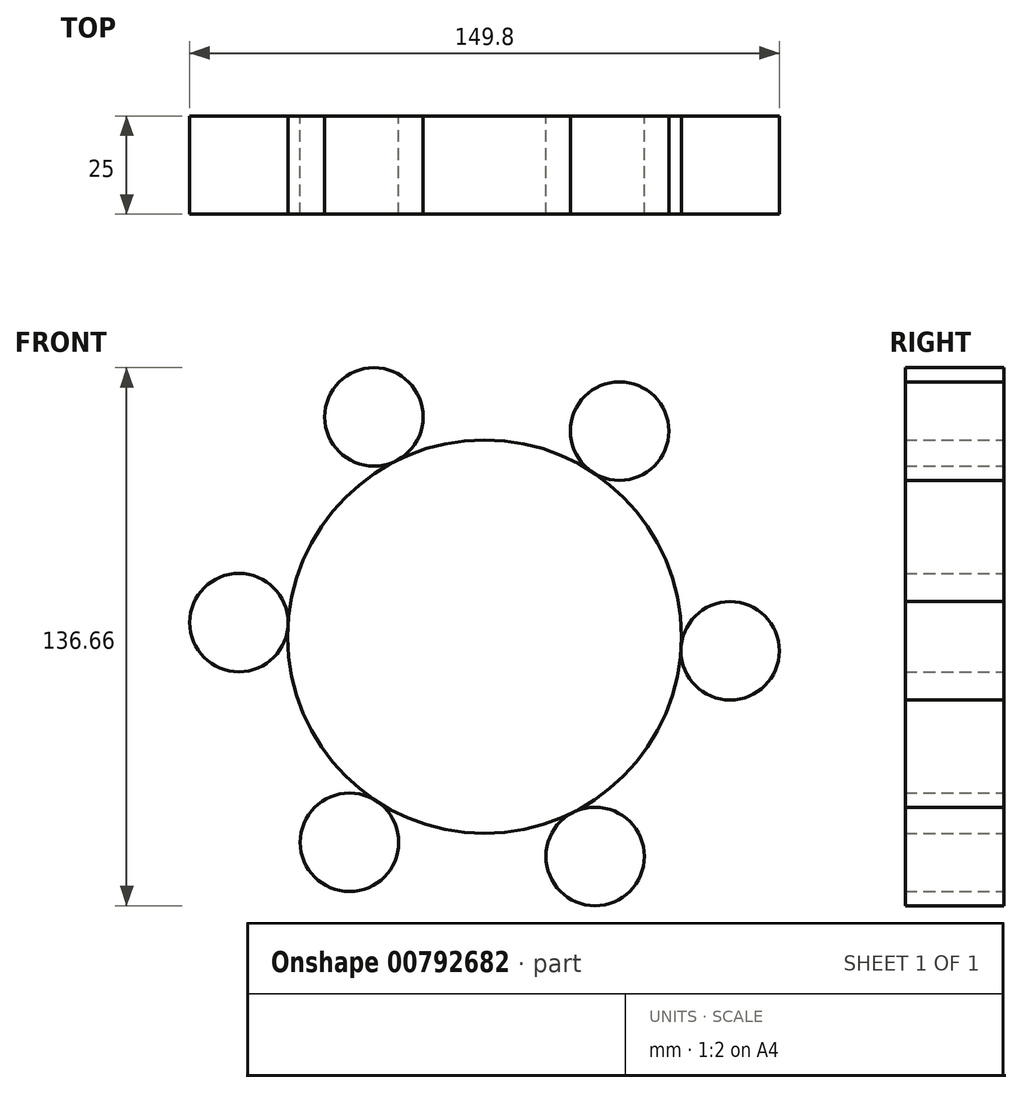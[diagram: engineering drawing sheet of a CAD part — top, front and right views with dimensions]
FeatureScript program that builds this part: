
annotation { "Feature Type Name" : "Feature", "Feature Type Description" : "" }
export const myFeature = defineFeature(function(context is Context, id is Id, definition is map)
    precondition{}
    {
        {
            var Q0;
            Q0=qCreatedBy(makeId("Front.planeOp"),FACE);
            var sketch = newSketch(context, id + "F0", { "sketchPlane" : qUnion([Q0])});
            skCircle(sketch, "E0", {"center": v(0, 0) * mm, "radius": 50 * mm});
            skSolve(sketch);
        }
        {
            var Q0;
            Q0=qCreatedBy(makeId("Front.planeOp"),FACE);
            var sketch = newSketch(context, id + "F1", { "sketchPlane" : qUnion([Q0])});
            skCircle(sketch, "E1", {"center": v(62.4, -3.59) * mm, "radius": 12.5 * mm});
            skSolve(sketch);
        }
        {
            var Q0;
            Q0=makeQuery(id+"F0.imprint","IMPRINT",FACE,{"disambiguationData":[TD([[makeQuery(id+"F0.imprint","IMPRINT",EDGE,{"derivedFrom":sQuery(id+"F0.wireOp",EDGE,"E0")}),1.0]])]});
            extrude(context, id + "F2", {"entities" : qUnion([Q0]), "depth" : 25 * mm, "offsetDistance" : 25 * mm});
        }
        {
            var Q0;
            Q0=makeQuery(id+"F1.imprint","IMPRINT",FACE,{"disambiguationData":[TD([[makeQuery(id+"F1.imprint","IMPRINT",EDGE,{"derivedFrom":sQuery(id+"F1.wireOp",EDGE,"E1")}),1.0]])]});
            extrude(context, id + "F3", {"entities" : qUnion([Q0]), "operationType" : NewBodyOperationType.ADD, "depth" : 25 * mm, "offsetDistance" : 25 * mm});
        }
        {
            var Q0;
            Q0=makeQuery(id+"F3.opExtrude","SWEPT_BODY",BODY,{"disambiguationData":[OSD([sQuery(id+"F1.wireOp",EDGE,"E1")])]});
            var Q1;
            Q1=makeQuery(id+"F2.opExtrude","CAP_EDGE",EDGE,{"disambiguationData":[OSD([sQuery(id+"F0.wireOp",EDGE,"E0")])],"isStart":false});
            circularPattern(context, id + "F4", {"entities" : qUnion([Q0]), "axis" : qUnion([Q1]), "angle" : 360 * degree, "instanceCount" : 6, "equalSpace" : true});
        }
    });
